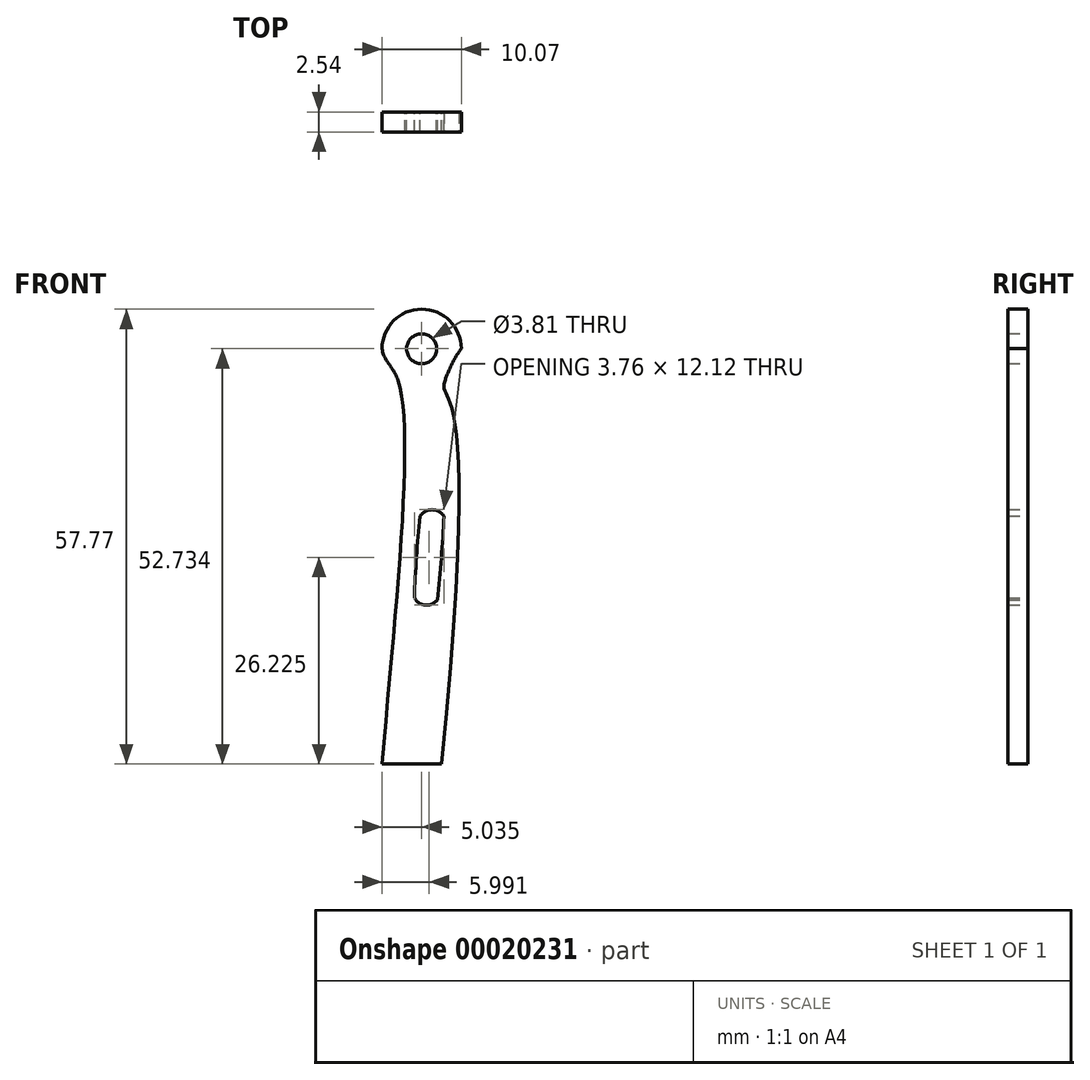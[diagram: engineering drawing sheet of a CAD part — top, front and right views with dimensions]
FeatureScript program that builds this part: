
annotation { "Feature Type Name" : "Feature", "Feature Type Description" : "" }
export const myFeature = defineFeature(function(context is Context, id is Id, definition is map)
    precondition{}
    {
        {
            var Q0;
            Q0=qCreatedBy(makeId("Front.planeOp"),FACE);
            var sketch = newSketch(context, id + "F0", { "sketchPlane" : qUnion([Q0])});
            skCircle(sketch, "E0", {"center": v(-0.47, 17.43) * mm, "radius": 1.9 * mm});
            skCircle(sketch, "E1", {"center": v(-0.47, 17.43) * mm, "radius": 3.81 * mm});
            skPoint(sketch, "E2.start.orphan", {"position": v(-0.47, 22.51) * mm});
            skArc(sketch, "E3", {"start": v(2.48, 13.36) * mm, "mid": v(-0.45, 22.47) * mm, "end": v(-3.48, 13.4) * mm});
            skLineSegment(sketch, "E4", {"start": v(-0.47, 17.43) * mm, "end": v(4.56, 17.43) * mm});
            skLineSegment(sketch, "E5", {"start": v(2.02, -35.3) * mm, "end": v(-5.51, -35.3) * mm});
            skFitSpline(sketch, "E6", {"points": [v(4.56, 17.43) * mm, v(2.48, 13.36) * mm, v(2.02, -35.3) * mm], "startDerivative": vector(-10.22, -11.95) * mm, "endDerivative": vector(-20.8, -203.64) * mm});
            skFitSpline(sketch, "E7", {"points": [v(-5.51, 17.43) * mm, v(-3.48, 13.4) * mm, v(-5.51, -35.3) * mm], "startDerivative": vector(3.56, -21.18) * mm, "endDerivative": vector(-7, -81.24) * mm});
            skArc(sketch, "E8", {"start": v(2.36, -3.84) * mm, "mid": v(0.84, -3.01) * mm, "end": v(-0.68, -3.84) * mm});
            skArc(sketch, "E9", {"start": v(-1.4, -14.22) * mm, "mid": v(0, -15.14) * mm, "end": v(1.53, -14.45) * mm});
            skArc(sketch, "E10", {"start": v(1.53, -14.45) * mm, "mid": v(2.02, -9.15) * mm, "end": v(2.36, -3.84) * mm});
            skArc(sketch, "E11", {"start": v(-0.68, -3.84) * mm, "mid": v(-1.14, -9.02) * mm, "end": v(-1.4, -14.22) * mm});
            skSolve(sketch);
        }
        {
            var Q0;
            Q0=makeQuery(id+"F0.imprint","IMPRINT",FACE,{"disambiguationData":[TD([[makeQuery(id+"F0.imprint","IMPRINT",EDGE,{"derivedFrom":sQuery(id+"F0.wireOp",EDGE,"E1")}),-1.0]])]});
            var Q1;
            Q1=makeQuery(id+"F0.imprint","IMPRINT",FACE,{"disambiguationData":[TD([[makeQuery(id+"F0.imprint","IMPRINT",EDGE,{"derivedFrom":sQuery(id+"F0.wireOp",EDGE,"E0")}),-1.0]])]});
            extrude(context, id + "F1", {"entities" : qUnion([Q0, Q1]), "depth" : 2.54 * mm});
        }
    });
